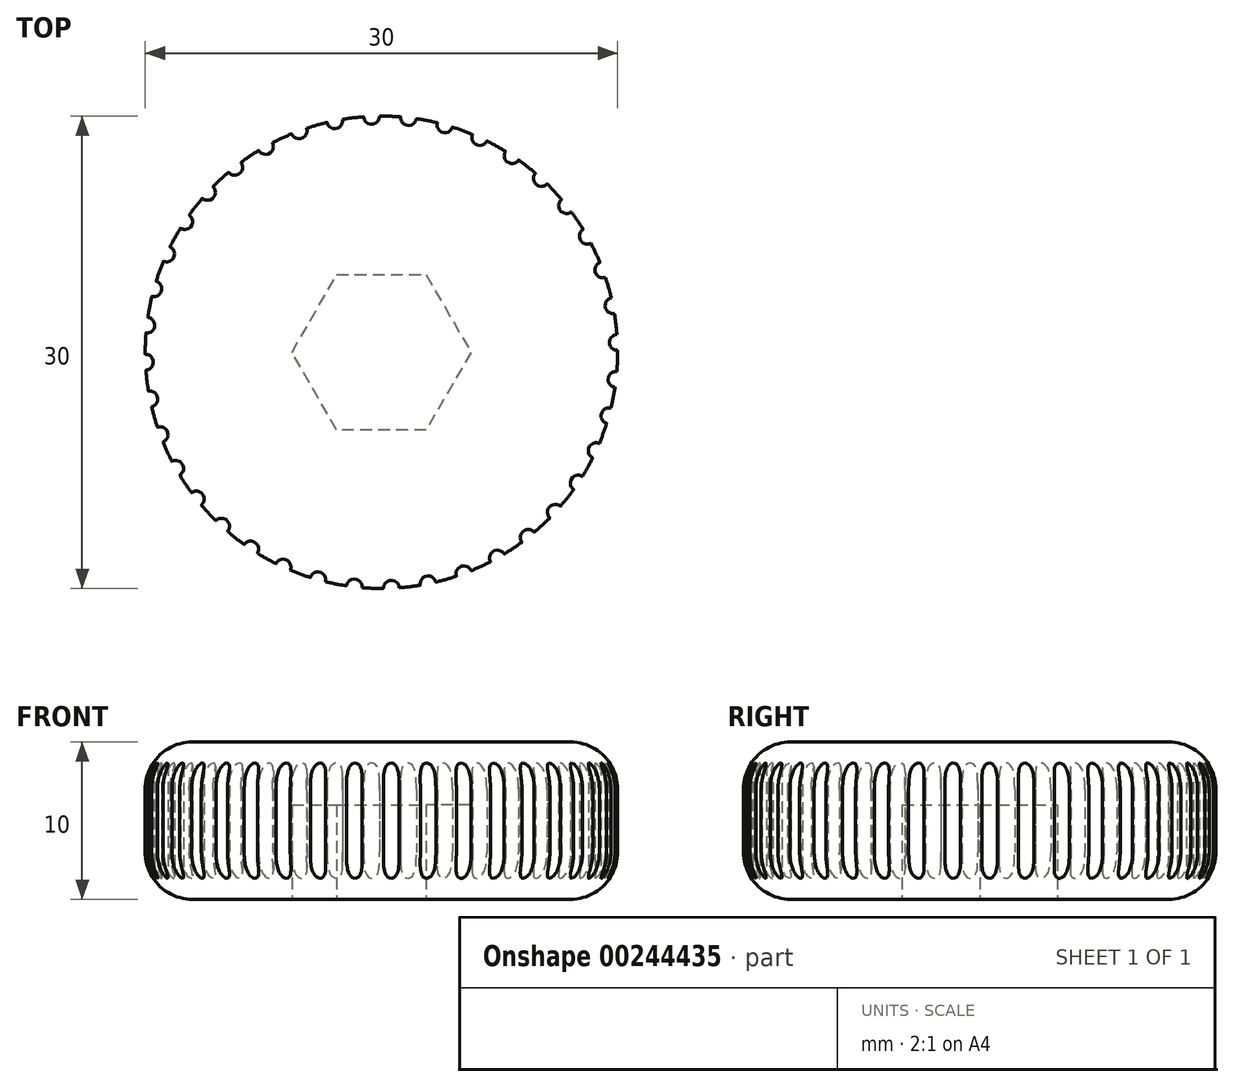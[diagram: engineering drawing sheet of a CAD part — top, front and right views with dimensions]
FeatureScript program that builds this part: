
annotation { "Feature Type Name" : "Feature", "Feature Type Description" : "" }
export const myFeature = defineFeature(function(context is Context, id is Id, definition is map)
    precondition{}
    {
        {
            var Q0;
            Q0=qCreatedBy(makeId("Top.planeOp"),FACE);
            var sketch = newSketch(context, id + "F0", { "sketchPlane" : qUnion([Q0])});
            skCircle(sketch, "E0.cCircle", {"center": v(0, 0) * mm, "radius": 4.92 * mm, "construction": true});
            skLineSegment(sketch, "E0.0", {"start": v(-2.84, 4.92) * mm, "end": v(2.84, 4.92) * mm});
            skLineSegment(sketch, "E0.1", {"start": v(2.84, 4.92) * mm, "end": v(5.69, 0) * mm});
            skLineSegment(sketch, "E0.2", {"start": v(5.69, 0) * mm, "end": v(2.84, -4.92) * mm});
            skLineSegment(sketch, "E0.3", {"start": v(2.84, -4.92) * mm, "end": v(-2.84, -4.93) * mm});
            skLineSegment(sketch, "E0.4", {"start": v(-2.84, -4.93) * mm, "end": v(-5.69, 0) * mm});
            skLineSegment(sketch, "E0.5", {"start": v(-5.69, 0) * mm, "end": v(-2.84, 4.92) * mm});
            skPoint(sketch, "E0.0.midPoint", {"position": v(0, 4.92) * mm});
            skCircle(sketch, "E1", {"center": v(0, 0) * mm, "radius": 15 * mm});
            skCircle(sketch, "E2", {"center": v(-8.3, -12.5) * mm, "radius": 0.5 * mm});
            skSolve(sketch);
        }
        {
            var Q0;
            Q0=makeQuery(id+"F0.imprint","IMPRINT",FACE,{"disambiguationData":[TD([[makeQuery(id+"F0.imprint","IMPRINT",EDGE,{"derivedFrom":sQuery(id+"F0.wireOp",EDGE,"E0.0")}),1.0]])]});
            var Q1;
            Q1=makeQuery(id+"F0.imprint","IMPRINT",FACE,{"disambiguationData":[TD([[makeQuery(id+"F0.imprint","IMPRINT",EDGE,{"derivedFrom":sQuery(id+"F0.wireOp",EDGE,"E0.0")}),-1.0]])]});
            extrude(context, id + "F1", {"entities" : qUnion([Q0, Q1]), "depth" : 10 * mm});
        }
        {
            var Q0;
            Q0=makeQuery(id+"F0.imprint","IMPRINT",FACE,{"disambiguationData":[TD([[makeQuery(id+"F0.imprint","IMPRINT",EDGE,{"derivedFrom":sQuery(id+"F0.wireOp",EDGE,"E0.0")}),-1.0]])]});
            extrude(context, id + "F2", {"entities" : qUnion([Q0]), "operationType" : NewBodyOperationType.REMOVE, "depth" : 6 * mm});
        }
        {
            var Q0;
            Q0=makeQuery(id+"F1.opExtrude","CAP_EDGE",EDGE,{"disambiguationData":[OSD([sQuery(id+"F0.wireOp",EDGE,"E1")])],"isStart":true});
            var Q1;
            Q1=makeQuery(id+"F1.opExtrude","CAP_EDGE",EDGE,{"disambiguationData":[OSD([sQuery(id+"F0.wireOp",EDGE,"E1")])],"isStart":false});
            fillet(context, id + "F3", {"entities" : qUnion([Q0, Q1]), "radius" : 3 * mm, "tangentPropagation" : true, "allowEdgeOverflow" : false});
        }
        {
            var Q0;
            {var subQ0=sQuery(id+"F0.wireOp",EDGE,"E2");var subQ1=sQuery(id+"F0.wireOp",EDGE,"E1");var subQ2=makeQuery(id+"F0.imprint","INTERSECT",VERTEX,{"disambiguationData":[OD(0.0)],"derivedFrom":[subQ1,subQ0]});Q0=makeQuery(id+"F0.imprint","IMPRINT",FACE,{"disambiguationData":[TD([[makeQuery(id+"F0.imprint","IMPRINT",EDGE,{"disambiguationData":[TD([[subQ2,-1.0]])],"derivedFrom":subQ1}),1.0]])]});}
            var Q1;
            {var subQ0=sQuery(id+"F0.wireOp",EDGE,"E2");var subQ1=sQuery(id+"F0.wireOp",EDGE,"E1");var subQ2=makeQuery(id+"F0.imprint","INTERSECT",VERTEX,{"disambiguationData":[OD(0.0)],"derivedFrom":[subQ1,subQ0]});Q1=makeQuery(id+"F0.imprint","IMPRINT",FACE,{"disambiguationData":[TD([[makeQuery(id+"F0.imprint","IMPRINT",EDGE,{"disambiguationData":[TD([[subQ2,-1.0]])],"derivedFrom":subQ1}),-1.0]])]});}
            var Q2;
            Q2=makeQuery(id+"F1.opExtrude","CAP_FACE",FACE,{"disambiguationData":[OSD([sQuery(id+"F0.wireOp",EDGE,"E1"),sQuery(id+"F0.wireOp",EDGE,"E2")])],"isStart":false});
            var Q3;
            Q3=makeQuery(id+"F1.opExtrude","SWEPT_BODY",BODY,{"disambiguationData":[OSD([sQuery(id+"F0.wireOp",EDGE,"E1"),sQuery(id+"F0.wireOp",EDGE,"E2")])]});
            extrude(context, id + "F4", {"entities" : qUnion([Q0, Q1]), "endBound" : BoundingType.UP_TO_SURFACE, "endBoundEntityFace" : qUnion([Q2]), "endBoundEntityBody" : qUnion([Q3]), "depth" : 25 * mm});
        }
        {
            var Q0;
            Q0=makeQuery(id+"F4.opExtrude","SWEPT_BODY",BODY,{"disambiguationData":[OSD([sQuery(id+"F0.wireOp",EDGE,"E2")])]});
            var Q1;
            {var subQ0=sQuery(id+"F0.wireOp",EDGE,"E1");Q1=makeQuery(id+"F3.opFillet","BLEND_EDGE",EDGE,{"blendedFrom":[makeQuery(id+"F1.opExtrude","CAP_EDGE",EDGE,{"disambiguationData":[OSD([subQ0])],"isStart":false}),makeQuery(id+"F1.opExtrude","CAP_FACE",FACE,{"disambiguationData":[OSD([subQ0,sQuery(id+"F0.wireOp",EDGE,"E2")])],"isStart":false})],"blendedInto":[makeQuery(id+"F1.opExtrude","CAP_FACE",FACE,{"disambiguationData":[OSD([subQ0,sQuery(id+"F0.wireOp",EDGE,"E2")])],"isStart":false})]});}
            circularPattern(context, id + "F5", {"operationType" : NewBodyOperationType.REMOVE, "entities" : qUnion([Q0]), "axis" : qUnion([Q1]), "angle" : 360 * degree, "instanceCount" : 40, "equalSpace" : true});
        }
    });
